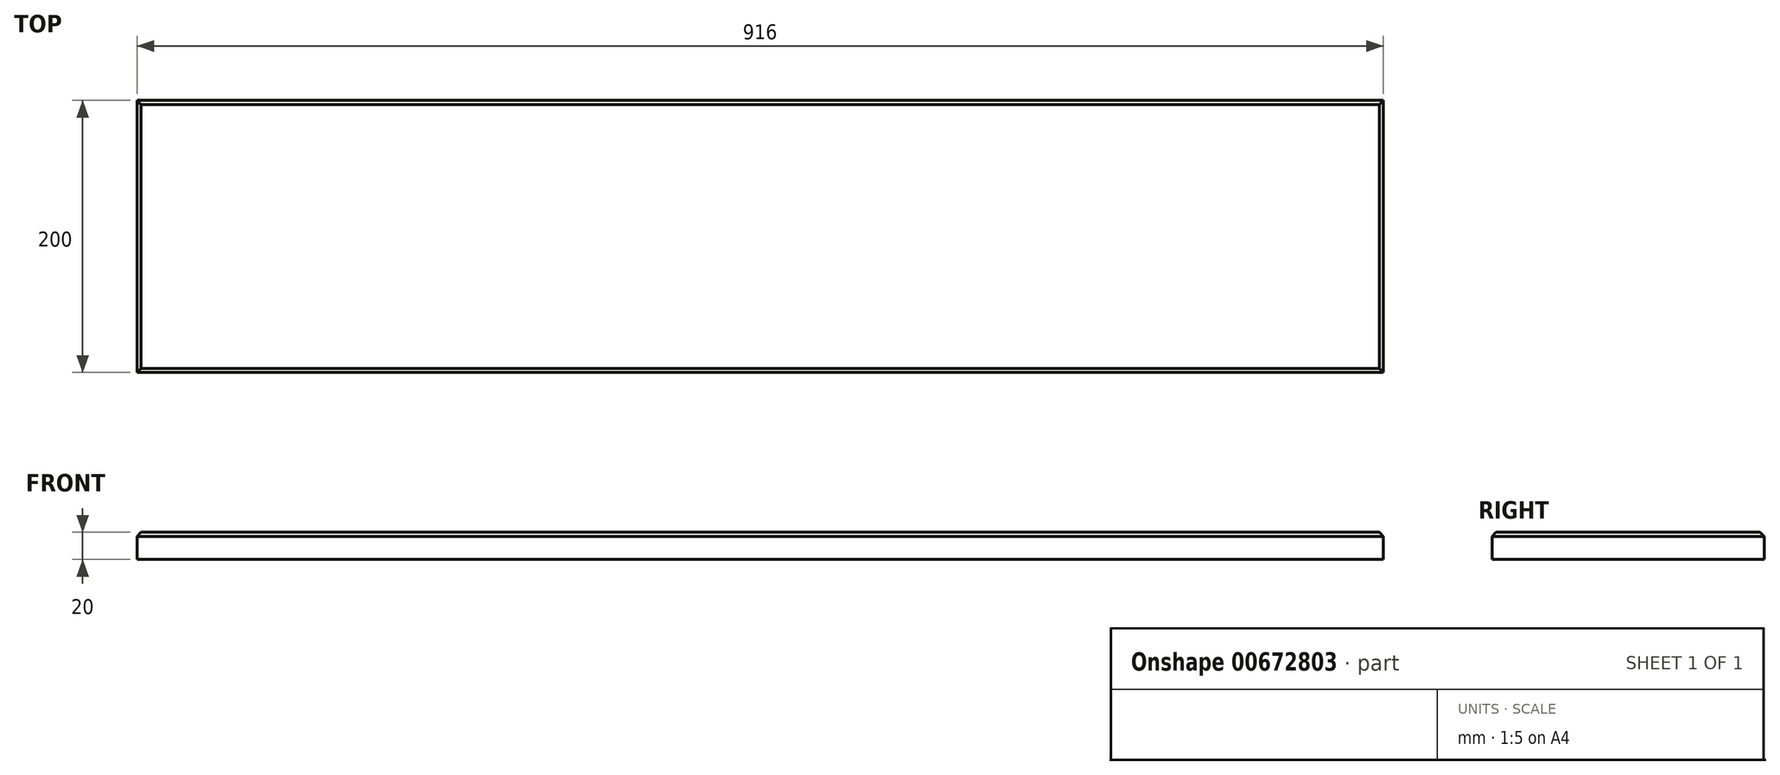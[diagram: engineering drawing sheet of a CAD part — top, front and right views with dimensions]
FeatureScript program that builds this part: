
annotation { "Feature Type Name" : "Feature", "Feature Type Description" : "" }
export const myFeature = defineFeature(function(context is Context, id is Id, definition is map)
    precondition{}
    {
        {
            var Q0;
            Q0=qCreatedBy(makeId("Top.planeOp"),FACE);
            var sketch = newSketch(context, id + "F0", { "sketchPlane" : qUnion([Q0])});
            skLineSegment(sketch, "E0.bottom", {"start": v(-458, 100) * mm, "end": v(458, 100) * mm});
            skLineSegment(sketch, "E0.top", {"start": v(-458, -100) * mm, "end": v(458, -100) * mm});
            skLineSegment(sketch, "E0.left", {"start": v(-458, 100) * mm, "end": v(-458, -100) * mm});
            skLineSegment(sketch, "E0.right", {"start": v(458, 100) * mm, "end": v(458, -100) * mm});
            skPoint(sketch, "E0.middle", {"position": v(0, 0) * mm});
            skSolve(sketch);
        }
        {
            var Q0;
            Q0 = qSketchRegion(id + "F0", true);
            extrude(context, id + "F1", {"entities" : qUnion([Q0]), "depth" : 20 * mm, "offsetDistance" : 25 * mm});
        }
        {
            var Q0;
            Q0=makeQuery(id+"F1.opExtrude","CAP_FACE",FACE,{"disambiguationData":[OSD([sQuery(id+"F0.wireOp",EDGE,"E0.bottom"),sQuery(id+"F0.wireOp",EDGE,"E0.top"),sQuery(id+"F0.wireOp",EDGE,"E0.left"),sQuery(id+"F0.wireOp",EDGE,"E0.right")])],"isStart":false});
            chamfer(context, id + "F2", {"entities" : qUnion([Q0]), "width" : 3 * mm, "tangentPropagation" : true});
        }
    });
